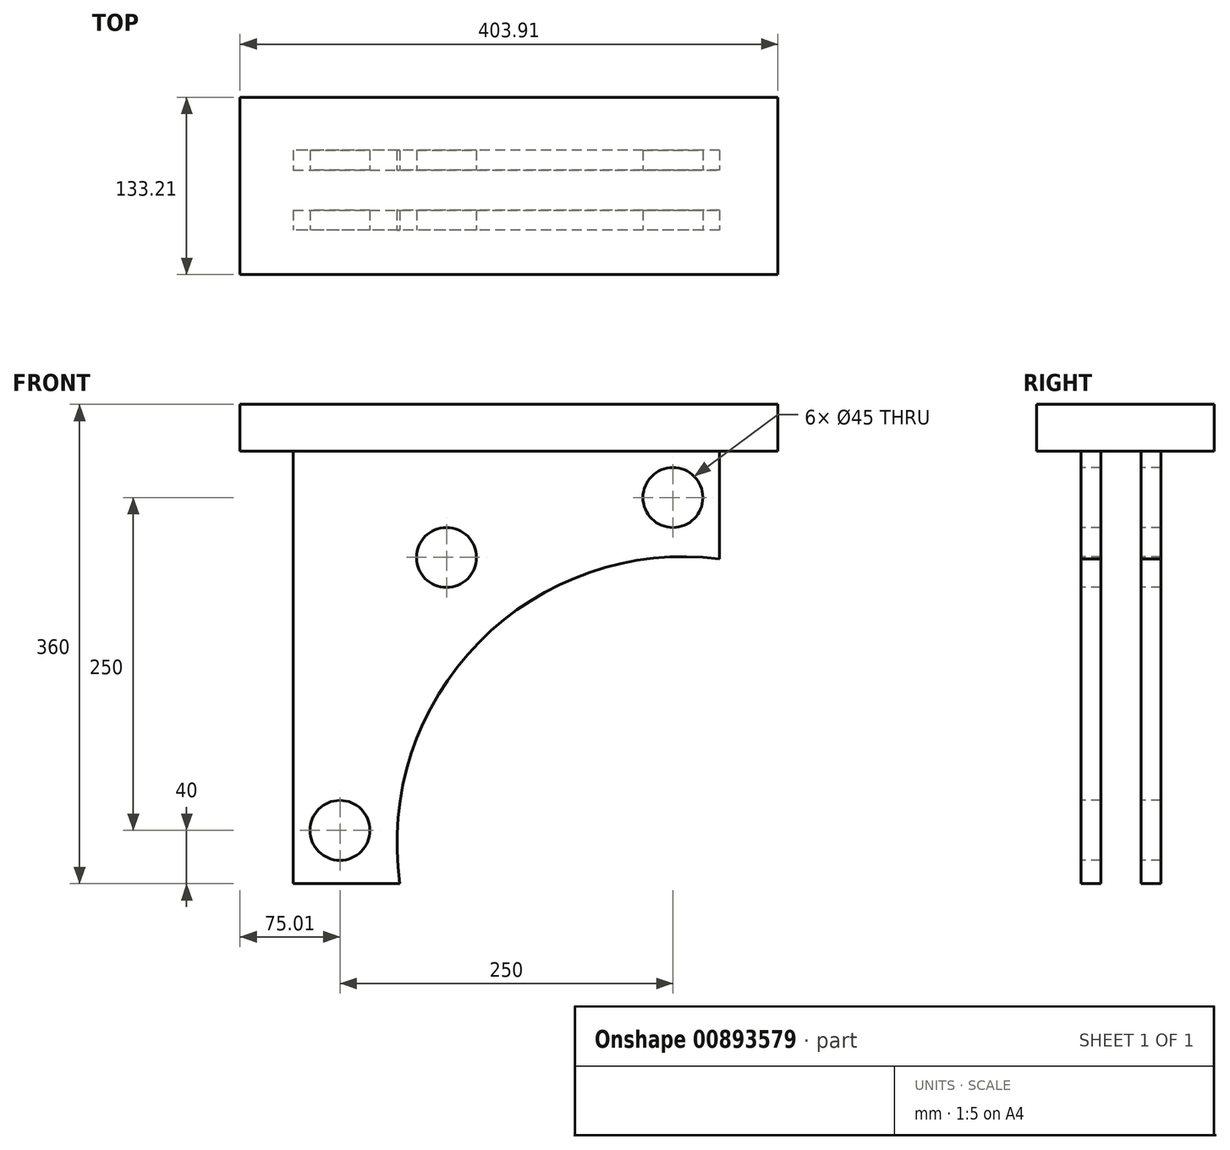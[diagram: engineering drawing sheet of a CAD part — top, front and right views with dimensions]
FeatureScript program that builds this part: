
annotation { "Feature Type Name" : "Feature", "Feature Type Description" : "" }
export const myFeature = defineFeature(function(context is Context, id is Id, definition is map)
    precondition{}
    {
        {
            var Q0;
            Q0=qCreatedBy(makeId("Top.planeOp"),FACE);
            var sketch = newSketch(context, id + "F0", { "sketchPlane" : qUnion([Q0])});
            skLineSegment(sketch, "E0.bottom", {"start": v(0, 24.73) * mm, "end": v(-320, 24.73) * mm});
            skLineSegment(sketch, "E0.top", {"start": v(0, -35.27) * mm, "end": v(-320, -35.27) * mm});
            skLineSegment(sketch, "E0.left", {"start": v(0, 24.73) * mm, "end": v(0, -35.27) * mm});
            skLineSegment(sketch, "E0.right", {"start": v(-320, 24.73) * mm, "end": v(-320, -35.27) * mm});
            skSolve(sketch);
        }
        {
            var Q0;
            Q0=qSketchRegion(id+"F0",true);
            extrude(context, id + "F1", {"entities" : qUnion([Q0]), "depth" : 360 * mm, "offsetDistance" : 25 * mm});
        }
        {
            var Q0;
            Q0=makeQuery(id+"F1.opExtrude","SWEPT_FACE",FACE,{"disambiguationData":[OSD([sQuery(id+"F0.wireOp",EDGE,"E0.top")])]});
            var sketch = newSketch(context, id + "F2", { "sketchPlane" : qUnion([Q0])});
            skCircle(sketch, "E1", {"center": v(-285, 40) * mm, "radius": 22.5 * mm});
            skCircle(sketch, "E2", {"center": v(-35, 290) * mm, "radius": 22.5 * mm});
            skCircle(sketch, "E3", {"center": v(-205, 245) * mm, "radius": 22.5 * mm});
            skSolve(sketch);
        }
        {
            var Q0;
            Q0=qSketchRegion(id+"F2",true);
            var Q1;
            Q1=makeQuery(id+"F1.opExtrude","SWEPT_FACE",FACE,{"disambiguationData":[OSD([sQuery(id+"F0.wireOp",EDGE,"E0.bottom")])]});
            extrude(context, id + "F3", {"entities" : qUnion([Q0]), "operationType" : NewBodyOperationType.REMOVE, "endBound" : BoundingType.UP_TO_SURFACE, "oppositeDirection" : true, "depth" : 25 * mm, "endBoundEntityFace" : qUnion([Q1]), "offsetDistance" : 25 * mm});
        }
        {
            var Q0;
            Q0=makeQuery(id+"F1.opExtrude","SWEPT_FACE",FACE,{"disambiguationData":[OSD([sQuery(id+"F0.wireOp",EDGE,"E0.top")])]});
            var sketch = newSketch(context, id + "F4", { "sketchPlane" : qUnion([Q0])});
            skLineSegment(sketch, "E4", {"start": v(-27.19, 30.58) * mm, "end": v(0, 243.86) * mm});
            skLineSegment(sketch, "E5", {"start": v(-27.19, 30.58) * mm, "end": v(-240, 0) * mm});
            skArc(sketch, "E6", {"start": v(0, 243.86) * mm, "mid": v(-180.42, 181.4) * mm, "end": v(-240, 0) * mm});
            skLineSegment(sketch, "E7", {"start": v(-320, 360) * mm, "end": v(0, 0) * mm, "construction": true});
            skSolve(sketch);
        }
        {
            var Q0;
            Q0=makeQuery(id+"F4.imprint","IMPRINT",FACE,{"disambiguationData":[TD([[makeQuery(id+"F4.imprint","IMPRINT",EDGE,{"derivedFrom":sQuery(id+"F4.wireOp",EDGE,"E4")}),-1.0]])]});
            var Q1;
            {var subQ5=sQuery(id+"F4.wireOp",EDGE,"E4");Q1=makeQuery(id+"F4.imprint","IMPRINT",FACE,{"disambiguationData":[TD([[makeQuery(id+"F4.imprint","IMPRINT",EDGE,{"derivedFrom":subQ5}),1.0]])]});}
            var Q2;
            Q2=makeQuery(id+"F1.opExtrude","SWEPT_FACE",FACE,{"disambiguationData":[OSD([sQuery(id+"F0.wireOp",EDGE,"E0.bottom")])]});
            extrude(context, id + "F5", {"entities" : qUnion([Q0, Q1]), "operationType" : NewBodyOperationType.REMOVE, "endBound" : BoundingType.UP_TO_SURFACE, "oppositeDirection" : true, "depth" : 25 * mm, "endBoundEntityFace" : qUnion([Q2]), "offsetDistance" : 25 * mm});
        }
        {
            var Q0;
            Q0=makeQuery(id+"F1.opExtrude","CAP_FACE",FACE,{"disambiguationData":[OSD([sQuery(id+"F0.wireOp",EDGE,"E0.bottom"),sQuery(id+"F0.wireOp",EDGE,"E0.top"),sQuery(id+"F0.wireOp",EDGE,"E0.left"),sQuery(id+"F0.wireOp",EDGE,"E0.right")])],"isStart":false});
            var sketch = newSketch(context, id + "F6", { "sketchPlane" : qUnion([Q0])});
            skLineSegment(sketch, "E8.bottom", {"start": v(-360.01, 64.58) * mm, "end": v(43.9, 64.58) * mm});
            skLineSegment(sketch, "E8.top", {"start": v(-360.01, -68.63) * mm, "end": v(43.9, -68.63) * mm});
            skLineSegment(sketch, "E8.left", {"start": v(-360.01, 64.58) * mm, "end": v(-360.01, -68.63) * mm});
            skLineSegment(sketch, "E8.right", {"start": v(43.9, 64.58) * mm, "end": v(43.9, -68.63) * mm});
            skSolve(sketch);
        }
        {
            var Q0;
            Q0=makeQuery(id+"F6.imprint","IMPRINT",FACE,{"disambiguationData":[TD([[makeQuery(id+"F6.imprint","IMPRINT",EDGE,{"derivedFrom":sQuery(id+"F6.wireOp",EDGE,"E8.bottom")}),-1.0]])]});
            extrude(context, id + "F7", {"entities" : qUnion([Q0]), "operationType" : NewBodyOperationType.ADD, "oppositeDirection" : true, "depth" : 35 * mm, "offsetDistance" : 25 * mm});
        }
        {
            var Q0;
            Q0=makeQuery(id+"F1.opExtrude","SWEPT_FACE",FACE,{"disambiguationData":[OSD([sQuery(id+"F0.wireOp",EDGE,"E0.left")])]});
            var sketch = newSketch(context, id + "F8", { "sketchPlane" : qUnion([Q0])});
            skLineSegment(sketch, "E9.bottom", {"start": v(-20.27, 0) * mm, "end": v(9.73, 0) * mm});
            skLineSegment(sketch, "E9.top", {"start": v(-20.27, 325) * mm, "end": v(9.73, 325) * mm});
            skLineSegment(sketch, "E9.left", {"start": v(9.73, 325) * mm, "end": v(9.73, 0) * mm});
            skLineSegment(sketch, "E9.right", {"start": v(-20.27, 325) * mm, "end": v(-20.27, 0) * mm});
            skSolve(sketch);
        }
        {
            var Q0;
            {var subQ0=sQuery(id+"F8.wireOp",EDGE,"E9.top");Q0=makeQuery(id+"F8.imprint","IMPRINT",FACE,{"disambiguationData":[TD([[makeQuery(id+"F8.imprint","IMPRINT",EDGE,{"derivedFrom":subQ0}),1.0]])]});}
            var Q1;
            {var subQ0=sQuery(id+"F8.wireOp",EDGE,"E9.bottom");Q1=makeQuery(id+"F8.imprint","IMPRINT",FACE,{"disambiguationData":[TD([[makeQuery(id+"F8.imprint","IMPRINT",EDGE,{"derivedFrom":subQ0}),1.0]])]});}
            var Q2;
            Q2=makeQuery(id+"F1.opExtrude","SWEPT_FACE",FACE,{"disambiguationData":[OSD([sQuery(id+"F0.wireOp",EDGE,"E0.right")])]});
            extrude(context, id + "F9", {"entities" : qUnion([Q0, Q1]), "operationType" : NewBodyOperationType.REMOVE, "endBound" : BoundingType.UP_TO_SURFACE, "oppositeDirection" : true, "depth" : 25 * mm, "endBoundEntityFace" : qUnion([Q2]), "offsetDistance" : 25 * mm});
        }
    });
